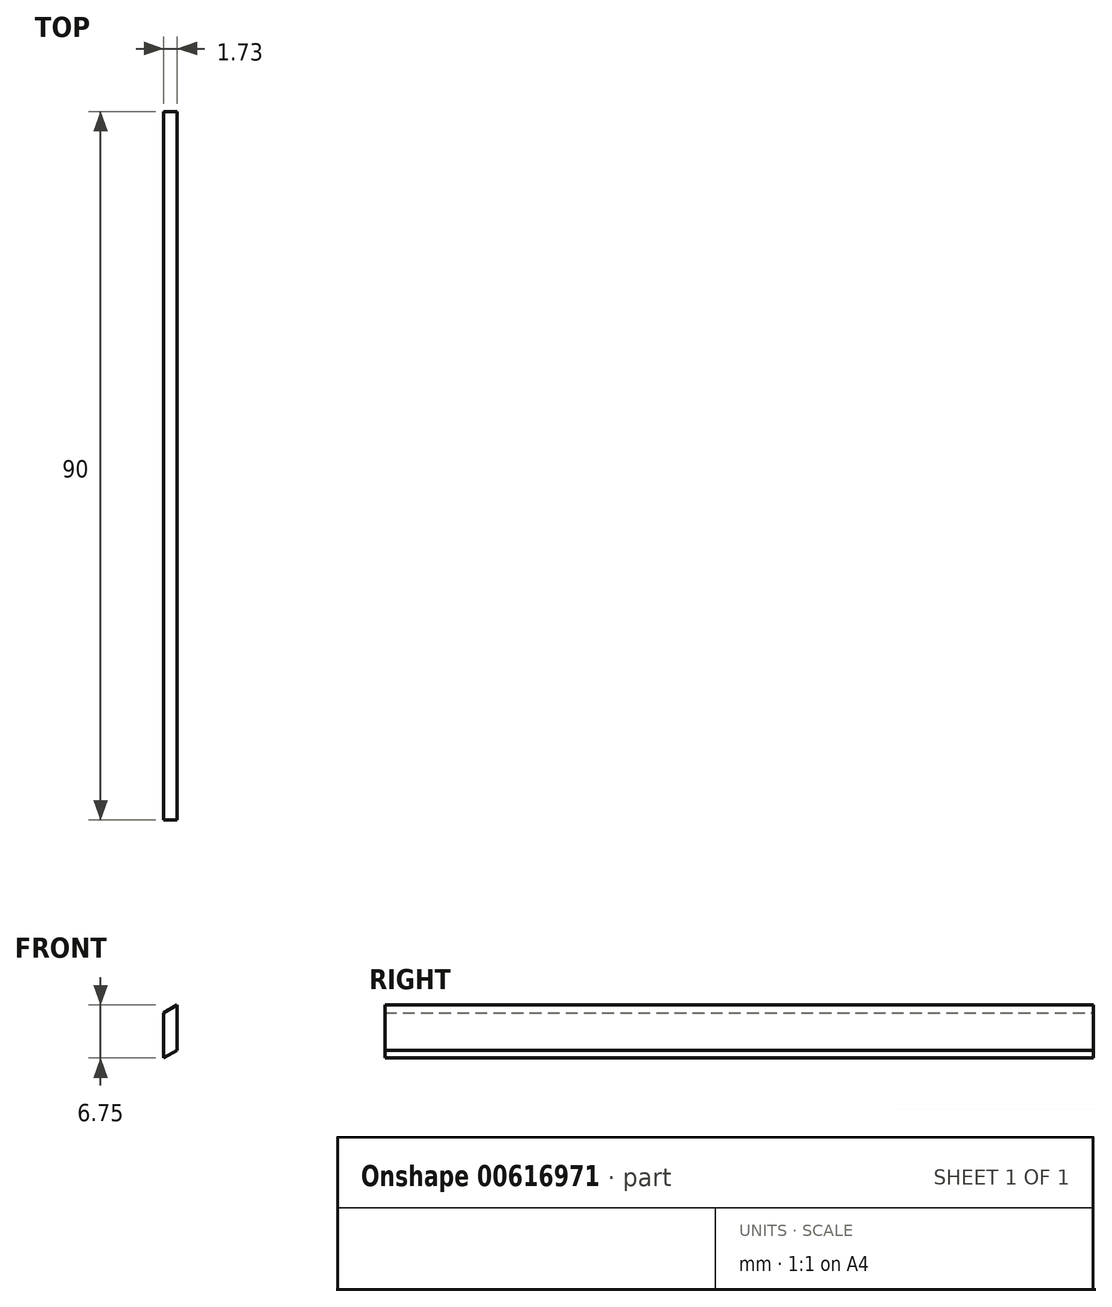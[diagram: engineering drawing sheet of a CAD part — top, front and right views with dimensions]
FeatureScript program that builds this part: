
annotation { "Feature Type Name" : "Feature", "Feature Type Description" : "" }
export const myFeature = defineFeature(function(context is Context, id is Id, definition is map)
    precondition{}
    {
        {
            var Q0;
            Q0=qCreatedBy(makeId("Front.planeOp"),FACE);
            var sketch = newSketch(context, id + "F0", { "sketchPlane" : qUnion([Q0])});
            skLineSegment(sketch, "E0", {"start": v(0, 0) * mm, "end": v(0, 5.75) * mm});
            skLineSegment(sketch, "E1", {"start": v(0, 0) * mm, "end": v(1.73, 1) * mm});
            skLineSegment(sketch, "E2", {"start": v(0, 5.75) * mm, "end": v(1.73, 6.75) * mm});
            skLineSegment(sketch, "E3", {"start": v(1.73, 1) * mm, "end": v(1.73, 6.75) * mm});
            skSolve(sketch);
        }
        {
            var Q0;
            Q0=makeQuery(id+"F0.imprint","IMPRINT",FACE,{"disambiguationData":[TD([[makeQuery(id+"F0.imprint","IMPRINT",EDGE,{"derivedFrom":sQuery(id+"F0.wireOp",EDGE,"VcbPU2CO-o5gd-ZBui-5XyG-Kp163W9YD6jG")}),1.0]])]});
            var Q1;
            Q1=makeQuery(id+"F0.imprint","IMPRINT",FACE,{"disambiguationData":[TD([[makeQuery(id+"F0.imprint","IMPRINT",EDGE,{"derivedFrom":sQuery(id+"F0.wireOp",EDGE,"E0")}),-1.0]])]});
            extrude(context, id + "F1", {"entities" : qUnion([Q0, Q1]), "depth" : 90 * mm, "offsetDistance" : 25 * mm});
        }
    });
